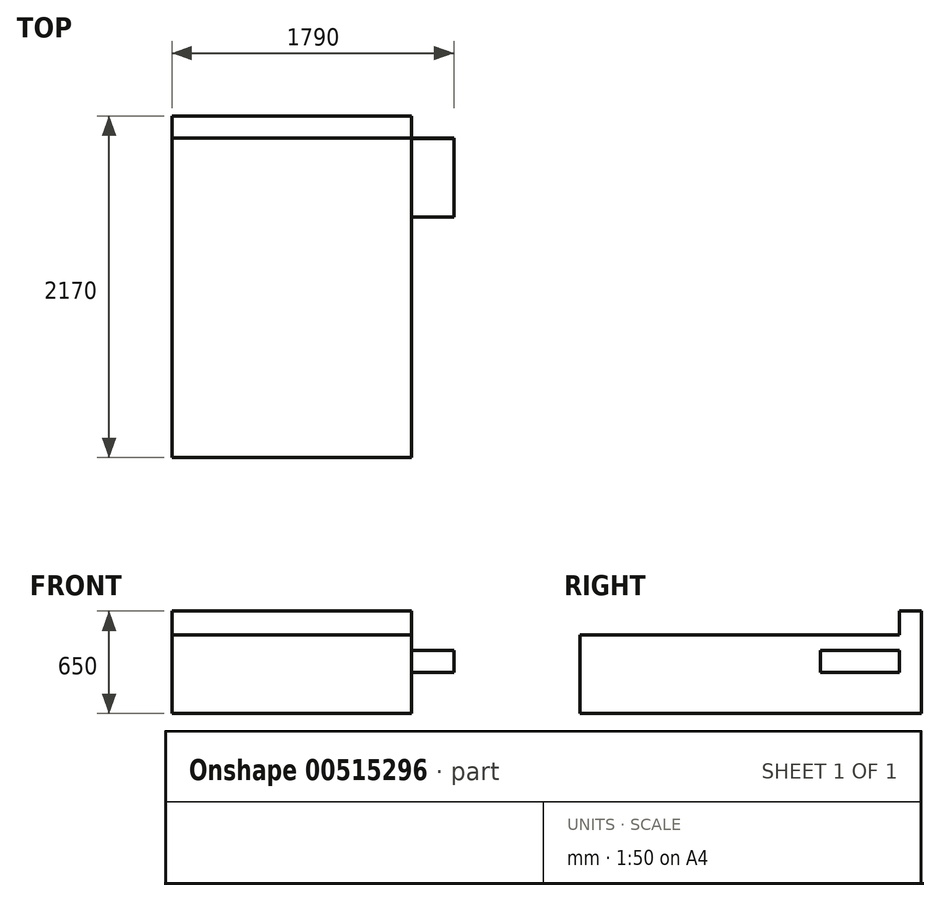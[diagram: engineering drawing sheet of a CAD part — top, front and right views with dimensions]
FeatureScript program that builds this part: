
annotation { "Feature Type Name" : "Feature", "Feature Type Description" : "" }
export const myFeature = defineFeature(function(context is Context, id is Id, definition is map)
    precondition{}
    {
        {
            var Q0;
            Q0=qCreatedBy(makeId("Front.planeOp"),FACE);
            var sketch = newSketch(context, id + "F0", { "sketchPlane" : qUnion([Q0])});
            skLineSegment(sketch, "E0.bottom", {"start": v(-760, 250) * mm, "end": v(760, 250) * mm});
            skLineSegment(sketch, "E0.top", {"start": v(-760, -250) * mm, "end": v(760, -250) * mm});
            skLineSegment(sketch, "E0.left", {"start": v(-760, 250) * mm, "end": v(-760, -250) * mm});
            skLineSegment(sketch, "E0.right", {"start": v(760, 250) * mm, "end": v(760, -250) * mm});
            skPoint(sketch, "E0.middle", {"position": v(0, 0) * mm});
            skSolve(sketch);
        }
        {
            var Q0;
            Q0 = qSketchRegion(id + "F0", true);
            extrude(context, id + "F1", {"entities" : qUnion([Q0]), "depth" : 2030 * mm, "offsetDistance" : 25 * mm});
        }
        {
            var Q0;
            Q0=makeQuery(id+"F1.opExtrude","CAP_FACE",FACE,{"disambiguationData":[OSD([sQuery(id+"F0.wireOp",EDGE,"E0.bottom"),sQuery(id+"F0.wireOp",EDGE,"E0.top"),sQuery(id+"F0.wireOp",EDGE,"E0.left"),sQuery(id+"F0.wireOp",EDGE,"E0.right")])],"isStart":true});
            var sketch = newSketch(context, id + "F2", { "sketchPlane" : qUnion([Q0])});
            skLineSegment(sketch, "E1.bottom", {"start": v(-760, -250) * mm, "end": v(760, -250) * mm});
            skLineSegment(sketch, "E1.top", {"start": v(-760, 400) * mm, "end": v(760, 400) * mm});
            skLineSegment(sketch, "E1.left", {"start": v(-760, -250) * mm, "end": v(-760, 400) * mm});
            skLineSegment(sketch, "E1.right", {"start": v(760, -250) * mm, "end": v(760, 400) * mm});
            skSolve(sketch);
        }
        {
            var Q0;
            Q0 = qSketchRegion(id + "F2", true);
            extrude(context, id + "F3", {"entities" : qUnion([Q0]), "depth" : 140 * mm, "offsetDistance" : 25 * mm});
        }
        {
            var Q0;
            Q0=makeQuery(id+"F1.opExtrude","SWEPT_FACE",FACE,{"disambiguationData":[OSD([sQuery(id+"F0.wireOp",EDGE,"E0.right")])]});
            var sketch = newSketch(context, id + "F4", { "sketchPlane" : qUnion([Q0])});
            skLineSegment(sketch, "E2.bottom", {"start": v(-1.81, 150) * mm, "end": v(-501.81, 150) * mm});
            skLineSegment(sketch, "E2.top", {"start": v(0, 10) * mm, "end": v(-501.81, 10) * mm});
            skLineSegment(sketch, "E2.right", {"start": v(-501.81, 150) * mm, "end": v(-501.81, 10) * mm});
            skLineSegment(sketch, "E3", {"start": v(0, 10) * mm, "end": v(-1.81, 150) * mm});
            skSolve(sketch);
        }
        {
            var Q0;
            Q0 = qSketchRegion(id + "F4", true);
            extrude(context, id + "F5", {"entities" : qUnion([Q0]), "operationType" : NewBodyOperationType.ADD, "depth" : 270 * mm, "offsetDistance" : 25 * mm});
        }
    });
